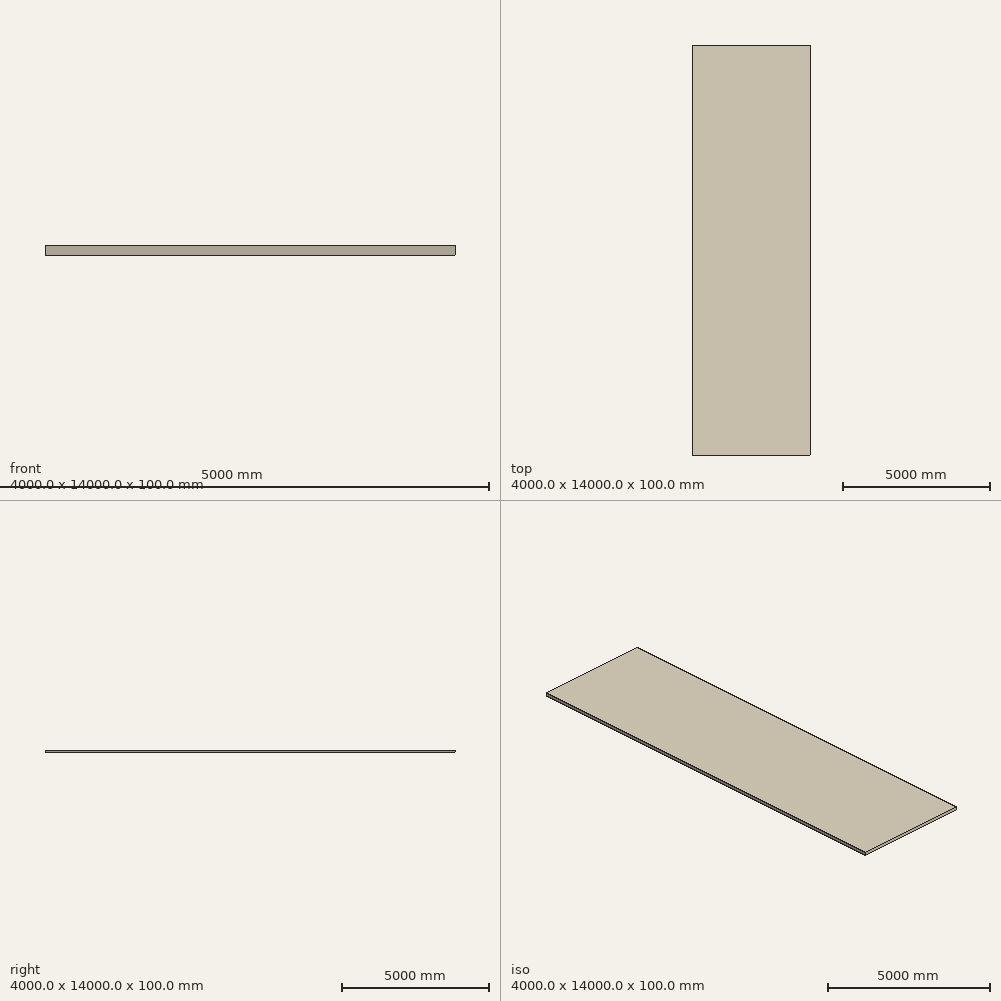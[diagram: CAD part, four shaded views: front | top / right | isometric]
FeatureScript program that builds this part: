
annotation { "Feature Type Name" : "Feature", "Feature Type Description" : "" }
export const myFeature = defineFeature(function(context is Context, id is Id, definition is map)
    precondition{}
    {
        {
            var Q0;
            Q0=qCreatedBy(makeId("Top.planeOp"),FACE);
            var sketch = newSketch(context, id + "F0", { "sketchPlane" : qUnion([Q0])});
            skLineSegment(sketch, "E0.bottom", {"start": v(-2000, 7000) * mm, "end": v(2000, 7000) * mm});
            skLineSegment(sketch, "E0.top", {"start": v(-2000, -7000) * mm, "end": v(2000, -7000) * mm});
            skLineSegment(sketch, "E0.left", {"start": v(-2000, 7000) * mm, "end": v(-2000, -7000) * mm});
            skLineSegment(sketch, "E0.right", {"start": v(2000, 7000) * mm, "end": v(2000, -7000) * mm});
            skSolve(sketch);
        }
        {
            var Q0;
            Q0 = qSketchRegion(id + "F0", true);
            extrude(context, id + "F1", {"entities" : qUnion([Q0]), "depth" : 100 * mm});
        }
    });
